# Revit family: Planet-Wattohm boites de sol charge lourde
name_source: partatom
category: Installations électriques
units: mm (PartAtom-declared; Revit-internal decimal feet)

## family parameters
Conserver l'orientation des annotations = Non
Cote de connecteur circulaire = Utiliser le diamètre
Couper avec des vides une fois chargée = Non
Hôte = Face
Partagée = Non
Point de calcul de pièce = Non
Type d'élément = Normal

## types (3) — shared parameters
Fabricant = PLANET WATTOHM
Heavy = Charge : Charge lourde
PW-28156 = Frame : PW-28156
Std = Charge : Charge standard
Type du sol = Charge : Charge standard
zero-valued in all types: Elévation par défaut

## per-type parameters (varying)
| type | Description | Frame | PW-28155 | PW-28158 | Supports |
| 24 modules sortie centrale | Charge lourde 24 modules avec sortie de câbles central | Frame : PW-28156 | Frame : PW-28155 | Frame : PW-28158 | PW-28156 |
| 24 modules sortie latérale | Charge lourde 24 modules avec sortie de câbles latérale | Frame : PW-28158 | Frame : PW-28156 | Frame : PW-28156 |  |
| Couvercle IP66 | Trappe d'accès charge lourde IP66 | Frame : PW-28155 | Frame : PW-28156 | Frame : PW-28156 |  |
